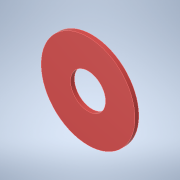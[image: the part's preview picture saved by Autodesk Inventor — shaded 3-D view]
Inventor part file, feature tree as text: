
AUTODESK INVENTOR PART (.ipt)
format: ipt  version: 2022.3 (Build 263350000, 350)  size: 111,104 bytes
history: native  units: in
note: dims shown in document units (in); Inventor stores cm internally (conversion verified against a paired STEP export)
features: sketch x1, extrude x1
ambient origin geometry x8: Origin, YZ Plane, XZ Plane, XY Plane, X Axis, Y Axis, Z Axis, Center Point
bodies: Solid1 (feature_tree)
feature tree (2):
  sketch  "Sketch1"  dims[d1=0.0625in d2=0.0in d13=0.561in d15=1.5in]
  extrude  "Extrusion1"  TaperAngle=0.0deg  [1 undecoded]
note: 1 required parameter value undecoded (feature->parameter linkage not recoverable at this tier; creation-order binding heuristic only, values carry confidence <= 0.55)
